# Revit family: Gymnasium_Equipment-Divider_Curtain-IPIbyBison-Walk_Draw-IP810
name_source: partatom
category: Specialty Equipment
units: mm (PartAtom-declared; Revit-internal decimal feet)

## family parameters
Always vertical = Yes
Classification Number = 23.40.50.34.17
Cut with Voids When Loaded = No
Enable Cutting in Views = No
Maintain Annotation Orientation = No
Part Type = Normal
Room Calculation Point = No
Round Connector Dimension = Use Diameter
Shared = No

## types (1)
- IP810
    Available Options = as Specified
    CAD Details = https://www.arcat.com
    Default Elevation = 0' - 0"
    Description = Gymnasium Roll Up Divider Curtain
    Keynote = 11 66 53
    Manufacturer = IPI by Bison
    Maximum Size = Contact Manufacturer for limits
    Model = IP810
    Product Page URL = https://www.arcat.com
    Specification = https://www.arcat.com
    URL = https://ipibybison.com

## geometry (parser evidence)
native form markers: Sweep x6
no freeform markers — native parametric forms only
